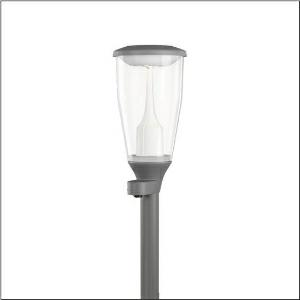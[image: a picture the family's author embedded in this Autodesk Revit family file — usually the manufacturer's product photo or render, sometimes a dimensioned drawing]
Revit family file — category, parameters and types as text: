
# Revit family: dl_11_iq___st1_2a_5xa5575eu14hp00022_2e6b
name_source: partatom
category: Lighting Fixtures
units: mm (PartAtom-declared; Revit-internal decimal feet)

## family parameters
Cut with Voids When Loaded = No
Host = Face
Light Source = No
Part Type = Normal
Room Calculation Point = No
Round Connector Dimension = Use Diameter
Shared = No

## types (1)
- --- (1 x LED, 4790 lm, 33.5 W, 3000K)
    Apparent Load = 34 VA
    CIE Flux Codes = 23 60 93 95 100
    Color Rendering = 70
    Color Temperature = 3000K
    Default Elevation = 1800 mm
    Description = DL 11 iQ, mast luminaire, Module 540 iQ-SR, primary light control with 3 zone facetted reflector, of plastic, silver coated, highly specular, structured, primary optical cover: cover, of PMMA, transparent, light distribution: ST1.2a, light emission: direct distribution, primary light characteristic: asymmetric, installation type: post-top, LED, High Power LED, rated luminous flux: 4.790lm, luminous efficacy: 143lm/W, light colour: 730, colour temperature: 3000K, control gear: iQ-Street Remote, D4i with power reduction, control: pre-setting: logarithmic dimming characteristic, Street-Remote, Auto-Match, Temp-Guard, Lumen-Switch, Night-Set, Smart-Wire, Light-Fading, Desk-Remote (wireless, voltage-free reading and setting of iQ features in the workshop via application-optimized NFC function/RFID function), optimised constant luminous flux control (CLO 2.0), mains connection: 220..240V, AC, 50/60Hz, connection cable pre-assembled, cable length: 5,5m, start of lifetime: 34W, end of service life: 36W, reduction: 15W, luminaire housing, upper part, of diecast aluminium, coated, SITECO metallic grey (DB 702S), spigot size: 76mm (post-top), mounting height: 3..5m, post-top mast mounting element, of diecast aluminium, coated, SITECO metallic grey (DB 702S), Module 540 iQ-SR, traffic white (RAL 9016), equipment: Power, Smart Interface below, protection rating (complete): IP66, insulation class (complete): insulation class II (safety insulation), certification: CE, ENEC, ENEC+, VDE, impact resistance: IK07, packaging unit: 1 piece

Light Distribution: ST1.2a
    Height = 665 mm
    Lamp = 1 x LED
    Lamp Light Flux = 4790 lm
    Lamp Power = 33.5 W
    Lamp count = 1
    Length = 334 mm
    Luminous efficacy = 143 lm/W
    Manufacturer = Siteco
    ModVariant = No
    Model = 5XA5575EU14HP00022
    Number of Poles = 1
    OnlyDefault = Yes
    Power Factor = 1
    Product Name = DL 11 iQ | ST1.2a
    Product group = mast luminaire | pylon top
    ProductGroupID = 6100
    Protection Class = Protection class II
    Protection Degree = IP 66
    RLX_Detail_Level = 1
    RLX_Emergency_Light_Flux = 0 lm
    RLX_Emergency_Type = 0
    RLX_Emergency_Type_DB = No
    RlxData = <blob elided: 160817 chars, md5=03d7e711>
    Socket = socket
    Standby Power = 0 W
    System Light Flux = 4790 lm
    System Power = 34 W
    Type Comments = factory setting: luminous flux: 100 % | dim-lin: 254 | 695 mA
    Type Image = l_1337539.jpg
    URL = http://relux.com
    VarID = @adj_040501
    Voltage = 0 V
    Weight = 0.00 kg
    Width = 0 mm  [stored 0 ft]

note: [stored X ft] marks values corroborated as IEEE doubles in the binary element streams (Revit-internal decimal feet)

## geometry (parser evidence)
native form markers: Blend x4, Sweep x9
no freeform markers — native parametric forms only
